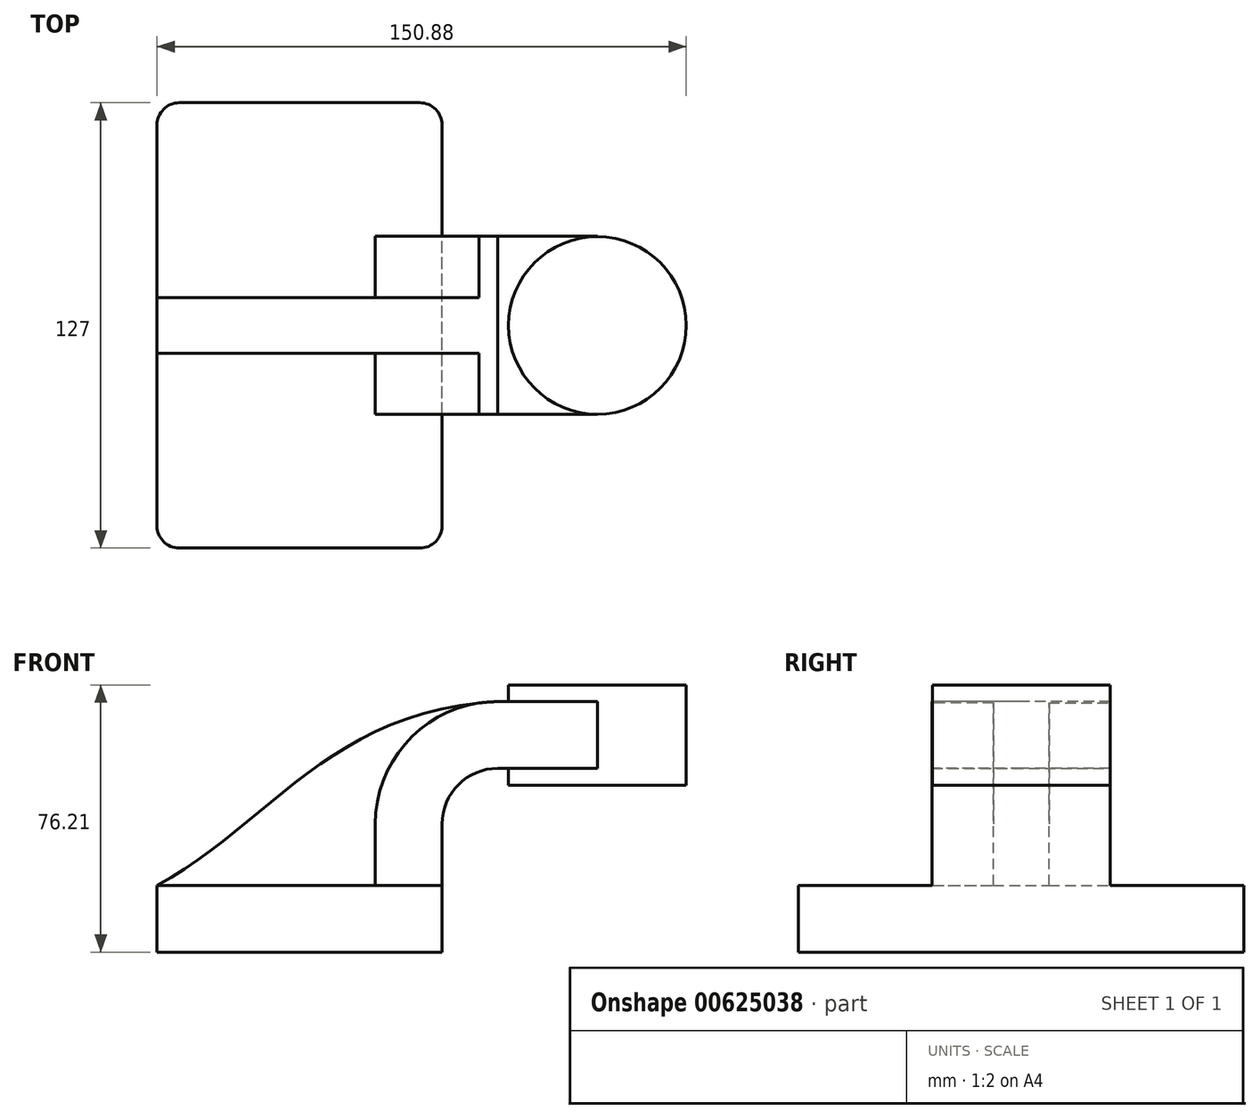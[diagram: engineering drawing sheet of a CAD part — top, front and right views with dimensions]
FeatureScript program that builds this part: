
annotation { "Feature Type Name" : "Feature", "Feature Type Description" : "" }
export const myFeature = defineFeature(function(context is Context, id is Id, definition is map)
    precondition{}
    {
        {
            var Q0;
            Q0=qCreatedBy(makeId("Front.planeOp"),FACE);
            var sketch = newSketch(context, id + "F0", { "sketchPlane" : qUnion([Q0])});
            skLineSegment(sketch, "E0.bottom", {"start": v(-40.64, -9.52) * mm, "end": v(40.64, -9.52) * mm});
            skLineSegment(sketch, "E0.top", {"start": v(-40.64, 9.53) * mm, "end": v(40.64, 9.53) * mm});
            skLineSegment(sketch, "E0.left", {"start": v(-40.64, -9.52) * mm, "end": v(-40.64, 9.53) * mm});
            skLineSegment(sketch, "E0.right", {"start": v(40.64, -9.52) * mm, "end": v(40.64, 9.53) * mm});
            skPoint(sketch, "E0.middle", {"position": v(0, 0) * mm});
            skLineSegment(sketch, "E1.bottom", {"start": v(59.44, 66.68) * mm, "end": v(110.24, 66.68) * mm});
            skLineSegment(sketch, "E1.top", {"start": v(59.44, 38.1) * mm, "end": v(110.24, 38.1) * mm});
            skLineSegment(sketch, "E1.left", {"start": v(59.44, 66.68) * mm, "end": v(59.44, 38.1) * mm});
            skLineSegment(sketch, "E1.right", {"start": v(110.24, 66.68) * mm, "end": v(110.24, 38.1) * mm});
            skPoint(sketch, "E1.middle", {"position": v(84.84, 52.39) * mm});
            skLineSegment(sketch, "E2", {"start": v(40.64, 9.53) * mm, "end": v(40.64, 27) * mm});
            skArc(sketch, "E3", {"start": v(40.64, 27) * mm, "mid": v(45.29, 38.23) * mm, "end": v(56.51, 42.88) * mm});
            skLineSegment(sketch, "E4", {"start": v(56.51, 42.88) * mm, "end": v(84.91, 42.88) * mm});
            skLineSegment(sketch, "E5.0", {"start": v(56.52, 61.93) * mm, "end": v(84.91, 61.93) * mm});
            skArc(sketch, "E5.1", {"start": v(21.59, 27) * mm, "mid": v(31.82, 51.7) * mm, "end": v(56.52, 61.93) * mm});
            skLineSegment(sketch, "E5.2", {"start": v(21.59, 9.53) * mm, "end": v(21.59, 27) * mm});
            skLineSegment(sketch, "E6", {"start": v(84.91, 61.93) * mm, "end": v(84.91, 42.88) * mm});
            skFitSpline(sketch, "E7", {"points": [v(-40.64, 9.53) * mm, v(56.52, 61.93) * mm], "startDerivative": vector(97.16, 52.4) * mm, "endDerivative": vector(143.64, 7.37) * mm});
            skLineSegment(sketch, "E8", {"start": v(84.91, 61.93) * mm, "end": v(84.91, 66.68) * mm});
            skLineSegment(sketch, "E9", {"start": v(84.91, 66.68) * mm, "end": v(84.91, 42.88) * mm});
            skLineSegment(sketch, "E10", {"start": v(84.91, 42.88) * mm, "end": v(84.91, 38.1) * mm});
            skSolve(sketch);
        }
        {
            var Q0;
            Q0=makeQuery(id+"F0.imprint","IMPRINT",FACE,{"disambiguationData":[TD([[makeQuery(id+"F0.imprint","IMPRINT",EDGE,{"derivedFrom":sQuery(id+"F0.wireOp",EDGE,"E0.bottom")}),1.0]])]});
            extrude(context, id + "F1", {"entities" : qUnion([Q0]), "endBound" : BoundingType.SYMMETRIC, "depth" : 127 * mm, "offsetDistance" : 25.4 * mm});
        }
        {
            var Q0;
            {var subQ1=sQuery(id+"F0.wireOp",EDGE,"E2");Q0=makeQuery(id+"F0.imprint","IMPRINT",FACE,{"disambiguationData":[TD([[makeQuery(id+"F0.imprint","IMPRINT",EDGE,{"derivedFrom":subQ1}),1.0]])]});}
            var Q1;
            {var subQ0=sQuery(id+"F0.wireOp",EDGE,"E5.0");var subQ1=sQuery(id+"F0.wireOp",EDGE,"E1.left");var subQ2=makeQuery(id+"F0.imprint","INTERSECT",VERTEX,{"derivedFrom":[subQ1,subQ0]});Q1=makeQuery(id+"F0.imprint","IMPRINT",FACE,{"disambiguationData":[TD([[makeQuery(id+"F0.imprint","IMPRINT",EDGE,{"disambiguationData":[TD([[subQ2,-1.0]])],"derivedFrom":subQ1}),1.0]])]});}
            extrude(context, id + "F2", {"entities" : qUnion([Q0, Q1]), "operationType" : NewBodyOperationType.ADD, "endBound" : BoundingType.SYMMETRIC, "depth" : 50.8 * mm, "offsetDistance" : 25.4 * mm});
        }
        {
            var Q0;
            {var subQ3=sQuery(id+"F0.wireOp",EDGE,"E5.2");Q0=makeQuery(id+"F0.imprint","IMPRINT",FACE,{"disambiguationData":[TD([[makeQuery(id+"F0.imprint","IMPRINT",EDGE,{"derivedFrom":subQ3}),1.0]])]});}
            extrude(context, id + "F3", {"entities" : qUnion([Q0]), "operationType" : NewBodyOperationType.ADD, "endBound" : BoundingType.SYMMETRIC, "depth" : 15.88 * mm, "offsetDistance" : 25.4 * mm});
        }
        {
            var Q0;
            {var subQ4=sQuery(id+"F0.wireOp",EDGE,"E1.right");Q0=makeQuery(id+"F0.imprint","IMPRINT",FACE,{"disambiguationData":[TD([[makeQuery(id+"F0.imprint","IMPRINT",EDGE,{"derivedFrom":subQ4}),-1.0]])]});}
            var Q1;
            Q1=sQuery(id+"F0.wireOp",EDGE,"E8");
            revolve(context, id + "F4", {"operationType" : NewBodyOperationType.ADD, "entities" : qUnion([Q0]), "axis" : qUnion([Q1]), "revolveType" : RevolveType.FULL});
        }
        {
            var Q0;
            Q0=makeQuery(id+"F1.opExtrude","CAP_EDGE",EDGE,{"disambiguationData":[OSD([sQuery(id+"F0.wireOp",EDGE,"E0.left")])],"isStart":false});
            var Q1;
            Q1=makeQuery(id+"F1.opExtrude","CAP_EDGE",EDGE,{"disambiguationData":[OSD([sQuery(id+"F0.wireOp",EDGE,"E0.right")])],"isStart":false});
            var Q2;
            Q2=makeQuery(id+"F1.opExtrude","CAP_EDGE",EDGE,{"disambiguationData":[OSD([sQuery(id+"F0.wireOp",EDGE,"E0.right")])],"isStart":true});
            var Q3;
            Q3=makeQuery(id+"F1.opExtrude","CAP_EDGE",EDGE,{"disambiguationData":[OSD([sQuery(id+"F0.wireOp",EDGE,"E0.left")])],"isStart":true});
            fillet(context, id + "F5", {"entities" : qUnion([Q0, Q1, Q2, Q3]), "radius" : 6.35 * mm, "tangentPropagation" : true, "allowEdgeOverflow" : false});
        }
    });
